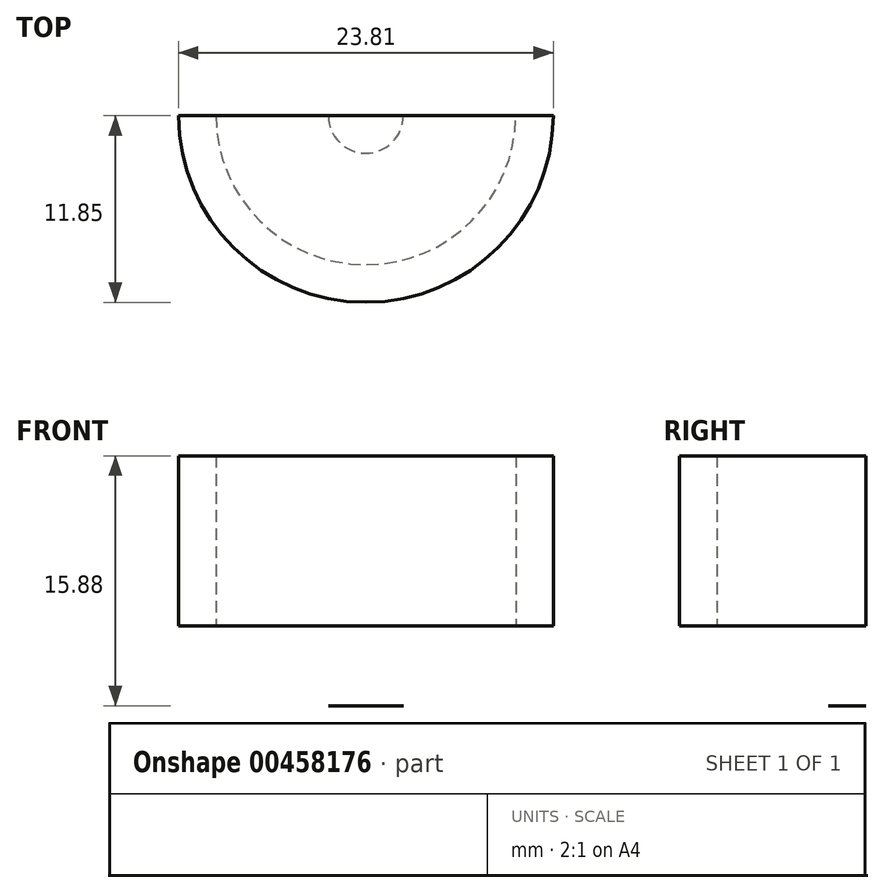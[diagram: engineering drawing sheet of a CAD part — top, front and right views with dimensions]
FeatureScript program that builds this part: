
annotation { "Feature Type Name" : "Feature", "Feature Type Description" : "" }
export const myFeature = defineFeature(function(context is Context, id is Id, definition is map)
    precondition{}
    {
        {
            var Q0;
            Q0=qCreatedBy(makeId("Top.planeOp"),FACE);
            var sketch = newSketch(context, id + "F0", { "sketchPlane" : qUnion([Q0])});
            skLineSegment(sketch, "E0", {"start": v(-8.11, 16.95) * mm, "end": v(15.7, 16.95) * mm});
            skArc(sketch, "E1", {"start": v(-8.11, 16.95) * mm, "mid": v(3.8, 5.1) * mm, "end": v(15.7, 16.95) * mm});
            skArc(sketch, "E2", {"start": v(-5.73, 16.95) * mm, "mid": v(3.8, 7.48) * mm, "end": v(13.32, 16.95) * mm});
            skSolve(sketch);
        }
        {
            var Q0;
            Q0=makeQuery(id+"F0.imprint","IMPRINT",FACE,{"disambiguationData":[TD([[makeQuery(id+"F0.imprint","IMPRINT",EDGE,{"derivedFrom":sQuery(id+"F0.wireOp",EDGE,"E0")}),-1.0]])]});
            extrude(context, id + "F1", {"entities" : qUnion([Q0]), "depth" : 15.88 * mm, "offsetDistance" : 25.4 * mm});
        }
        {
            var Q0;
            {var subQ0=sQuery(id+"F0.wireOp",EDGE,"E2");Q0=makeQuery(id+"F0.imprint","IMPRINT",FACE,{"disambiguationData":[TD([[makeQuery(id+"F0.imprint","IMPRINT",EDGE,{"derivedFrom":subQ0}),1.0]])]});}
            extrude(context, id + "F2", {"entities" : qUnion([Q0]), "operationType" : NewBodyOperationType.ADD, "depth" : 1 / 812.8 * mm});
        }
        {
            var Q0;
            Q0=makeQuery(id+"F1.opExtrude","CAP_FACE",FACE,{"disambiguationData":[OSD([sQuery(id+"F0.wireOp",EDGE,"E0"),sQuery(id+"F0.wireOp",EDGE,"E1"),sQuery(id+"F0.wireOp",EDGE,"E2")])],"isStart":false});
            var sketch = newSketch(context, id + "F3", { "sketchPlane" : qUnion([Q0])});
            skLineSegment(sketch, "E3", {"start": v(-5.73, 16.95) * mm, "end": v(13.32, 16.95) * mm});
            skArc(sketch, "E4", {"start": v(-5.73, 16.95) * mm, "mid": v(3.8, 7.42) * mm, "end": v(13.32, 16.95) * mm});
            skLineSegment(sketch, "E5", {"start": v(-8.11, 16.95) * mm, "end": v(-5.73, 16.95) * mm});
            skArc(sketch, "E6", {"start": v(-8.11, 16.95) * mm, "mid": v(3.8, 5.04) * mm, "end": v(15.7, 16.95) * mm});
            skSolve(sketch);
        }
        {
            var Q0;
            Q0 = qSketchRegion(id + "F3", true);
            var Q1;
            Q1=makeQuery(id+"F3.imprint","IMPRINT",FACE,{"disambiguationData":[TD([[makeQuery(id+"F3.imprint","IMPRINT",EDGE,{"derivedFrom":sQuery(id+"F3.wireOp",EDGE,"E4")}),-1.0]])]});
            extrude(context, id + "F4", {"entities" : qUnion([Q0, Q1]), "operationType" : NewBodyOperationType.ADD, "depth" : 1 / 812.8 * mm, "offsetDistance" : 25.4 * mm});
        }
        {
            var Q0;
            {var subQ0=sQuery(id+"F0.wireOp",EDGE,"E2");var subQ1=sQuery(id+"F0.wireOp",EDGE,"E0");Q0=makeQuery(id+"F2.boolean.opBoolean","MERGE",FACE,{"derivedFrom":[makeQuery(id+"F1.opExtrude","CAP_FACE",FACE,{"disambiguationData":[OSD([subQ1,sQuery(id+"F0.wireOp",EDGE,"E1"),subQ0])],"isStart":true}),makeQuery(id+"F2.opExtrude","CAP_FACE",FACE,{"disambiguationData":[OSD([subQ1,subQ0])],"isStart":true})]});}
            var sketch = newSketch(context, id + "F5", { "sketchPlane" : qUnion([Q0])});
            skArc(sketch, "E7", {"start": v(1.41, -16.95) * mm, "mid": v(3.8, -14.57) * mm, "end": v(6.17, -16.95) * mm});
            skSolve(sketch);
        }
        {
            var Q0;
            {var subQ0=sQuery(id+"F5.wireOp",EDGE,"E7");Q0=makeQuery(id+"F5.imprint","IMPRINT",FACE,{"disambiguationData":[TD([[makeQuery(id+"F5.imprint","IMPRINT",EDGE,{"derivedFrom":subQ0}),-1.0]])]});}
            extrude(context, id + "F6", {"entities" : qUnion([Q0]), "operationType" : NewBodyOperationType.REMOVE, "oppositeDirection" : true, "depth" : 5.08 * mm, "offsetDistance" : 25.4 * mm});
        }
    });
